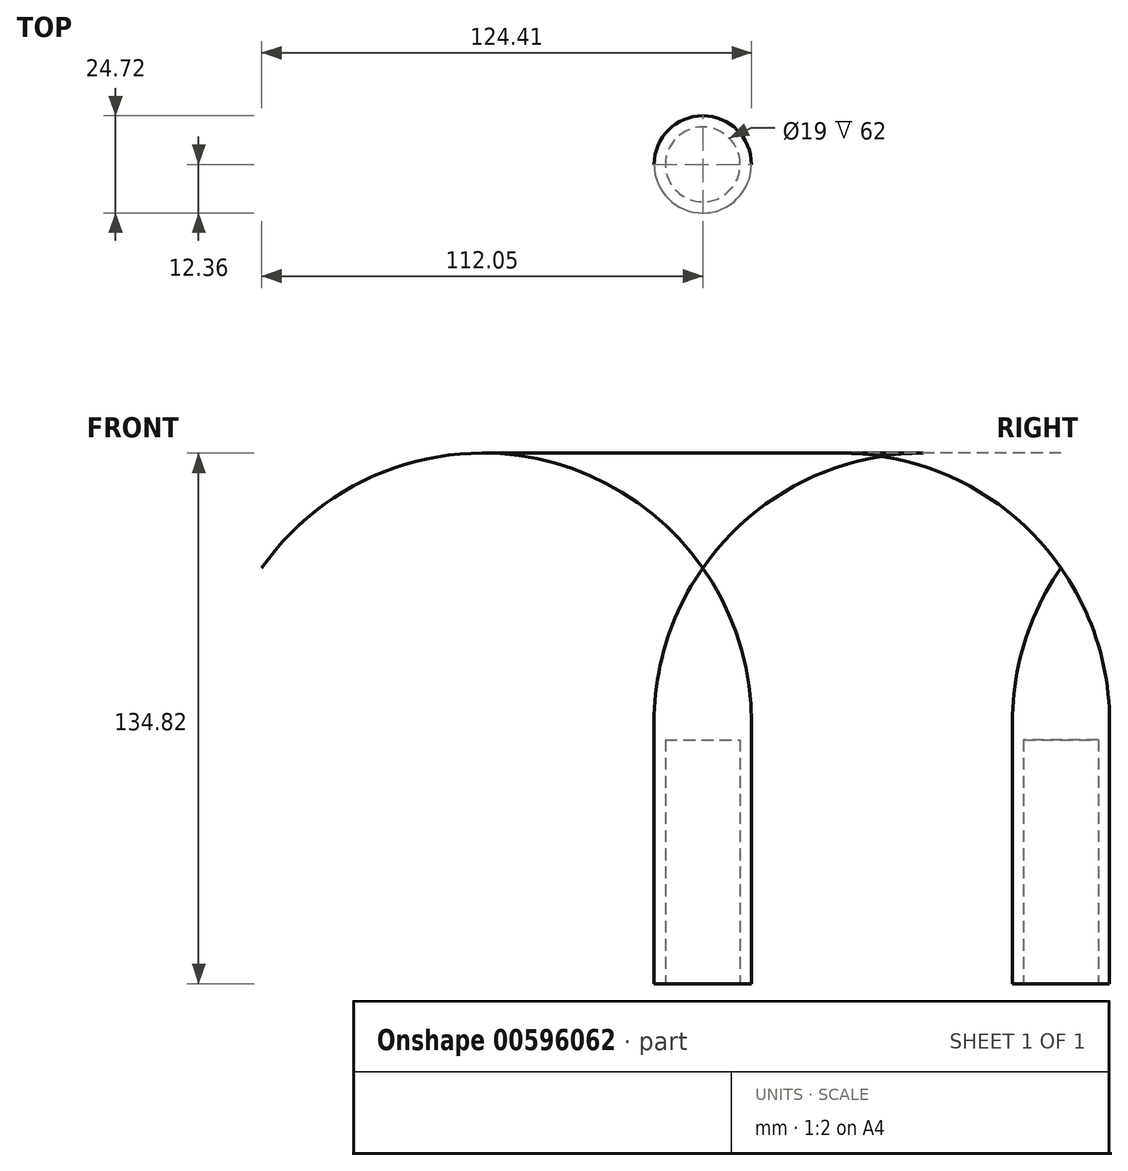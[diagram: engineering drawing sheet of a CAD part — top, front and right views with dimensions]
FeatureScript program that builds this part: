
annotation { "Feature Type Name" : "Feature", "Feature Type Description" : "" }
export const myFeature = defineFeature(function(context is Context, id is Id, definition is map)
    precondition{}
    {
        {
            var Q0;
            Q0=qCreatedBy(makeId("Right.planeOp"),FACE);
            var sketch = newSketch(context, id + "F0", { "sketchPlane" : qUnion([Q0])});
            skLineSegment(sketch, "E0.bottom", {"start": v(0, 0) * mm, "end": v(12.36, 0) * mm});
            skLineSegment(sketch, "E0.left", {"start": v(0, 0) * mm, "end": v(0, 66.44) * mm});
            skLineSegment(sketch, "E0.right", {"start": v(12.36, 0) * mm, "end": v(12.36, 66.44) * mm});
            skLineSegment(sketch, "E1", {"start": v(0, 66.44) * mm, "end": v(0, 105.65) * mm});
            skArc(sketch, "E2", {"start": v(12.36, 66.44) * mm, "mid": v(9.2, 87) * mm, "end": v(0, 105.65) * mm});
            skLineSegment(sketch, "E3", {"start": v(9.5, 0) * mm, "end": v(9.5, 62) * mm});
            skLineSegment(sketch, "E4", {"start": v(9.5, 62) * mm, "end": v(9.5, 0) * mm});
            skLineSegment(sketch, "E5", {"start": v(9.5, 62) * mm, "end": v(0, 62) * mm});
            skLineSegment(sketch, "E6", {"start": v(0, 62) * mm, "end": v(9.5, 62) * mm});
            skSolve(sketch);
        }
        {
            var Q0;
            {var subQ1=sQuery(id+"F0.wireOp",EDGE,"E0.right");Q0=makeQuery(id+"F0.imprint","IMPRINT",FACE,{"disambiguationData":[TD([[makeQuery(id+"F0.imprint","IMPRINT",EDGE,{"derivedFrom":subQ1}),1.0]])]});}
            var Q1;
            Q1=sQuery(id+"F0.wireOp",EDGE,"E1");
            revolve(context, id + "F1", {"entities" : qUnion([Q0]), "axis" : qUnion([Q1]), "revolveType" : RevolveType.FULL});
        }
    });
